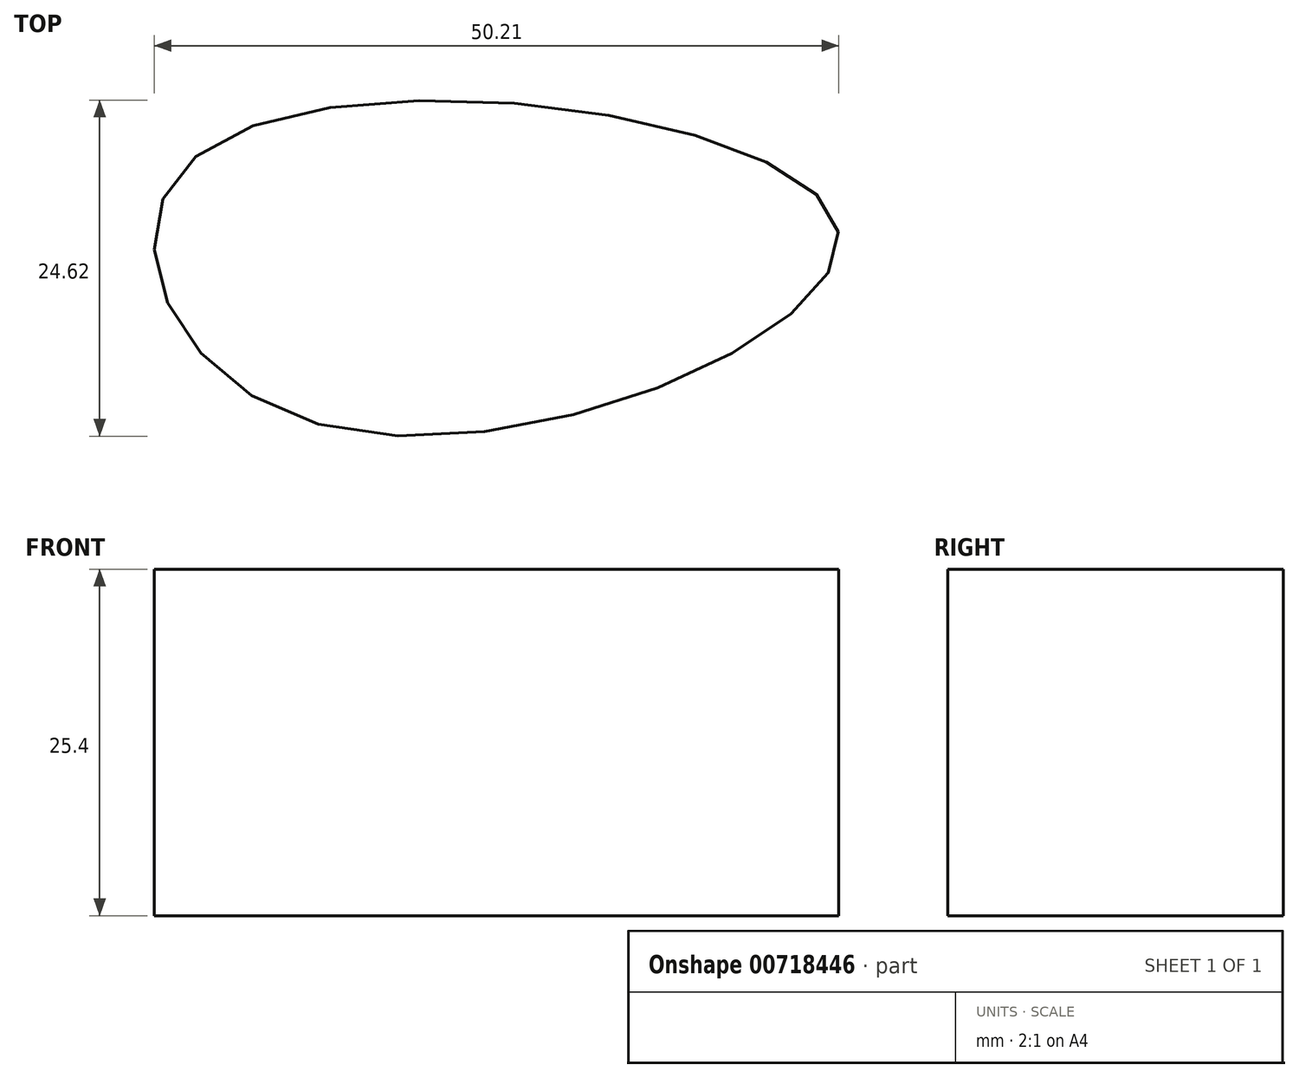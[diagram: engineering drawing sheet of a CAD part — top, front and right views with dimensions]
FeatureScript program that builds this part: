
annotation { "Feature Type Name" : "Feature", "Feature Type Description" : "" }
export const myFeature = defineFeature(function(context is Context, id is Id, definition is map)
    precondition{}
    {
        {
            var Q0;
            Q0=qCreatedBy(makeId("Top.planeOp"),FACE);
            var sketch = newSketch(context, id + "F0", { "sketchPlane" : qUnion([Q0])});
            skFitSpline(sketch, "E0", {"points": [v(-27.32, 55) * mm, v(19.72, 49.94) * mm, v(-18.64, 35.46) * mm, v(-27.32, 55) * mm]});
            skSolve(sketch);
        }
        {
            var Q0;
            Q0 = qSketchRegion(id + "F0", true);
            extrude(context, id + "F1", {"entities" : qUnion([Q0]), "depth" : 25.4 * mm, "offsetDistance" : 25.4 * mm});
        }
    });
